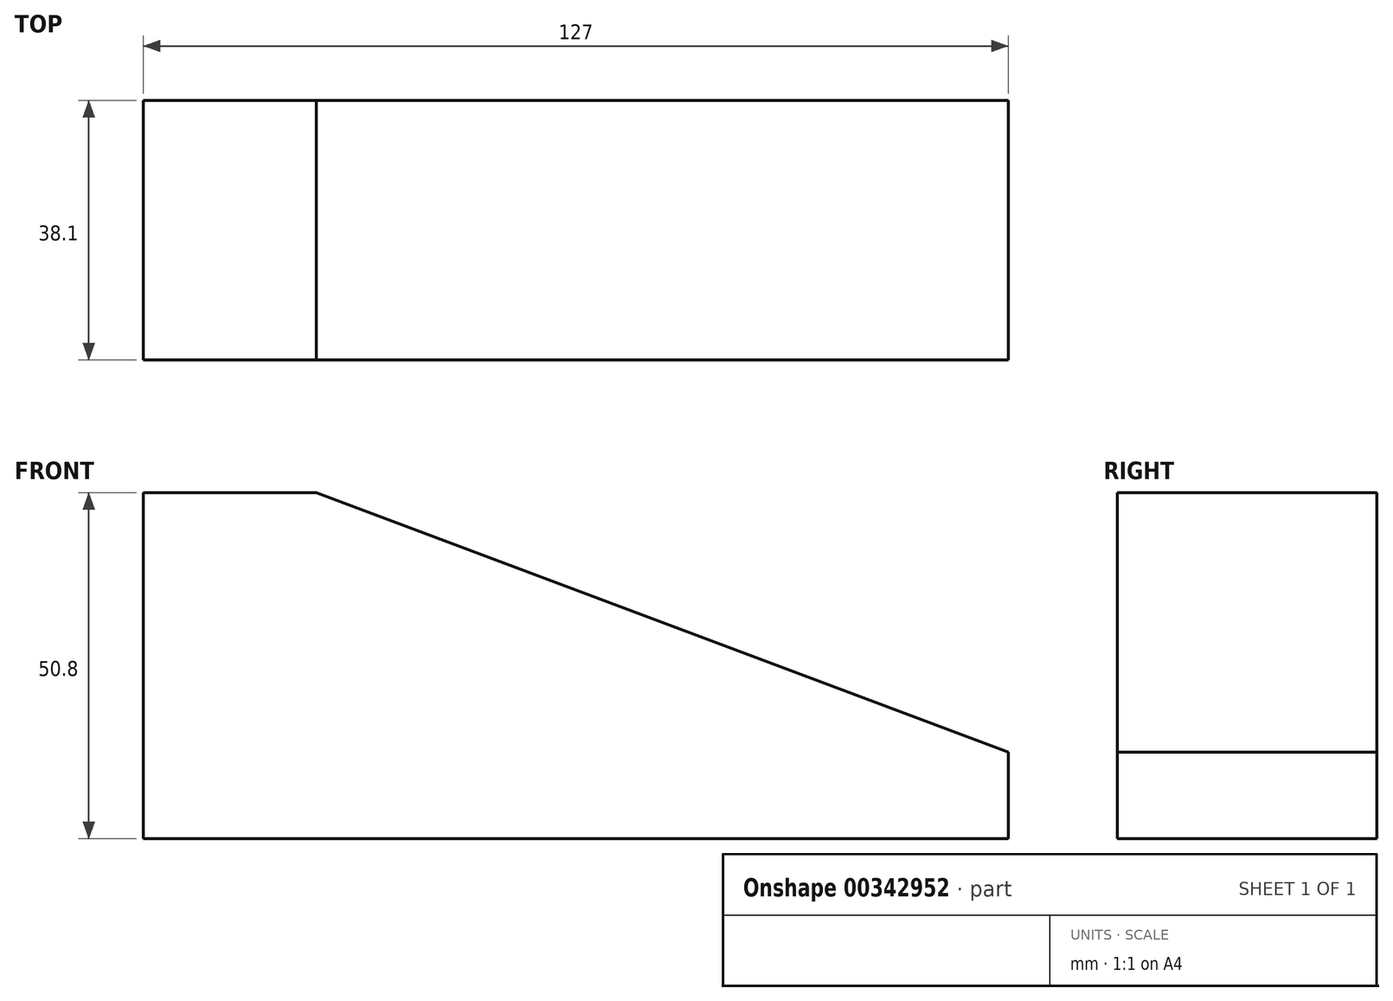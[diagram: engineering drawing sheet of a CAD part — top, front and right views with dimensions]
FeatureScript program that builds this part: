
annotation { "Feature Type Name" : "Feature", "Feature Type Description" : "" }
export const myFeature = defineFeature(function(context is Context, id is Id, definition is map)
    precondition{}
    {
        {
            var Q0;
            Q0=qCreatedBy(makeId("Front.planeOp"),FACE);
            var sketch = newSketch(context, id + "F0", { "sketchPlane" : qUnion([Q0])});
            skLineSegment(sketch, "E0", {"start": v(-25.4, 13.92) * mm, "end": v(0, 13.92) * mm});
            skLineSegment(sketch, "E1", {"start": v(-25.4, 13.92) * mm, "end": v(-25.4, -36.88) * mm});
            skLineSegment(sketch, "E2", {"start": v(-25.4, -36.88) * mm, "end": v(101.6, -36.88) * mm});
            skLineSegment(sketch, "E3", {"start": v(101.6, -36.88) * mm, "end": v(101.6, -24.18) * mm});
            skLineSegment(sketch, "E4", {"start": v(0, 13.92) * mm, "end": v(101.6, -24.18) * mm});
            skSolve(sketch);
        }
        {
            var Q0;
            Q0=makeQuery(id+"F0.imprint","IMPRINT",FACE,{"disambiguationData":[TD([[makeQuery(id+"F0.imprint","IMPRINT",EDGE,{"derivedFrom":sQuery(id+"F0.wireOp",EDGE,"E0")}),-1.0]])]});
            extrude(context, id + "F1", {"entities" : qUnion([Q0]), "depth" : 38.1 * mm});
        }
    });
